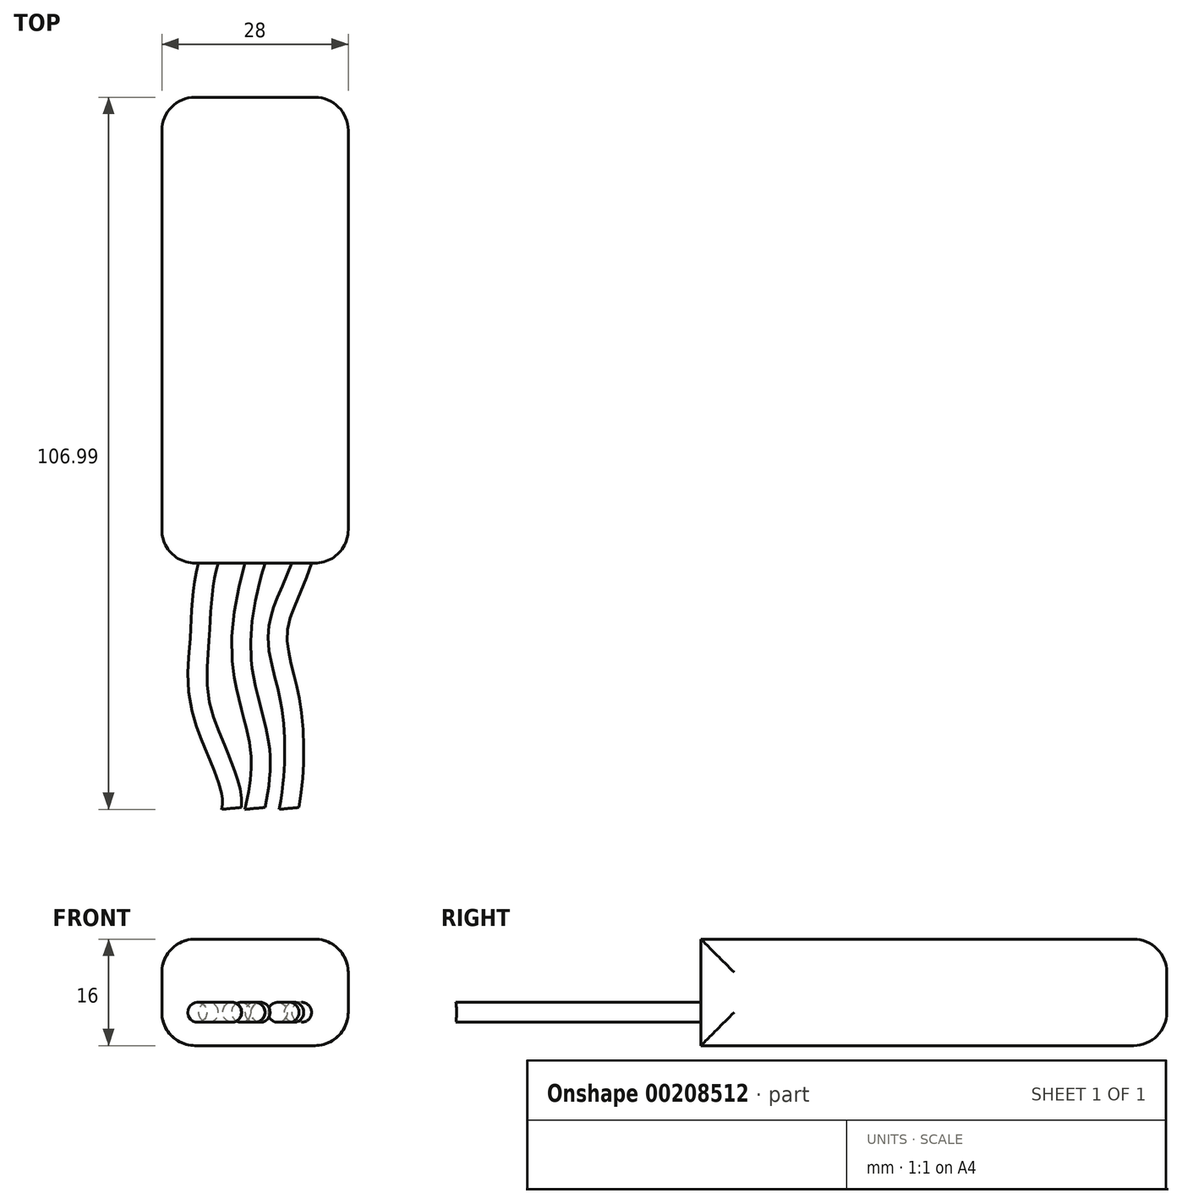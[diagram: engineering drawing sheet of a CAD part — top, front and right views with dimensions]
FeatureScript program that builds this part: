
annotation { "Feature Type Name" : "Feature", "Feature Type Description" : "" }
export const myFeature = defineFeature(function(context is Context, id is Id, definition is map)
    precondition{}
    {
        {
            var Q0;
            Q0=qCreatedBy(makeId("Top.planeOp"),FACE);
            var sketch = newSketch(context, id + "F0", { "sketchPlane" : qUnion([Q0])});
            skLineSegment(sketch, "E0.bottom", {"start": v(14, -35) * mm, "end": v(-14, -35) * mm});
            skLineSegment(sketch, "E0.top", {"start": v(14, 35) * mm, "end": v(-14, 35) * mm});
            skLineSegment(sketch, "E0.left", {"start": v(14, -35) * mm, "end": v(14, 35) * mm});
            skLineSegment(sketch, "E0.right", {"start": v(-14, -35) * mm, "end": v(-14, 35) * mm});
            skPoint(sketch, "E0.middle", {"position": v(0, 0) * mm});
            skSolve(sketch);
        }
        {
            var Q0;
            Q0 = qSketchRegion(id + "F0", true);
            extrude(context, id + "F1", {"entities" : qUnion([Q0]), "depth" : 16 * mm});
        }
        {
            var Q0;
            Q0=makeQuery(id+"F1.opExtrude","SWEPT_FACE",FACE,{"disambiguationData":[OSD([sQuery(id+"F0.wireOp",EDGE,"E0.left")])]});
            var Q1;
            Q1=makeQuery(id+"F1.opExtrude","SWEPT_FACE",FACE,{"disambiguationData":[OSD([sQuery(id+"F0.wireOp",EDGE,"E0.right")])]});
            var Q2;
            Q2=makeQuery(id+"F1.opExtrude","SWEPT_FACE",FACE,{"disambiguationData":[OSD([sQuery(id+"F0.wireOp",EDGE,"E0.top")])]});
            fillet(context, id + "F2", {"entities" : qUnion([Q0, Q1, Q2]), "radius" : 5 * mm, "tangentPropagation" : true, "allowEdgeOverflow" : false});
        }
        {
            var Q0;
            Q0=makeQuery(id+"F1.opExtrude","SWEPT_FACE",FACE,{"disambiguationData":[OSD([sQuery(id+"F0.wireOp",EDGE,"E0.bottom")])]});
            var sketch = newSketch(context, id + "F3", { "sketchPlane" : qUnion([Q0])});
            skCircle(sketch, "E1", {"center": v(0, 5) * mm, "radius": 1.5 * mm});
            skCircle(sketch, "E2", {"center": v(7, 5) * mm, "radius": 1.5 * mm});
            skCircle(sketch, "E3", {"center": v(-7, 5) * mm, "radius": 1.5 * mm});
            skSolve(sketch);
        }
        {
            var Q0;
            Q0=makeQuery(id+"F1.opExtrude","CAP_FACE",FACE,{"disambiguationData":[OSD([sQuery(id+"F0.wireOp",EDGE,"E0.bottom"),sQuery(id+"F0.wireOp",EDGE,"E0.top"),sQuery(id+"F0.wireOp",EDGE,"E0.left"),sQuery(id+"F0.wireOp",EDGE,"E0.right")])],"isStart":false});
            var Q1;
            Q1=sQuery(id+"F3.wireOp",VERTEX,"E1.center");
            cPlane(context, id + "F4", {"entities" : qUnion([Q0, Q1]), "cplaneType" : CPlaneType.PLANE_POINT, "offset" : 25 * mm, "width" : 150 * mm, "height" : 150 * mm});
        }
        {
            var Q0;
            Q0=qCreatedBy(id+"F4.planeOp",FACE);
            var sketch = newSketch(context, id + "F5", { "sketchPlane" : qUnion([Q0])});
            skFitSpline(sketch, "E4", {"points": [v(0, -35) * mm, v(-2, -49.56) * mm, v(0.74, -62.9) * mm, v(0, -71.85) * mm], "startDerivative": vector(-10.09, -32.94) * mm, "endDerivative": vector(-5.76, -27.82) * mm});
            skFitSpline(sketch, "E5", {"points": [v(-7, -35) * mm, v(-8.33, -46.63) * mm, v(-7.9, -57.6) * mm, v(-3.53, -71.85) * mm], "startDerivative": vector(-10.09, -32.94) * mm, "endDerivative": vector(-5.76, -27.82) * mm});
            skFitSpline(sketch, "E6", {"points": [v(7, -35) * mm, v(3.45, -45.1) * mm, v(5.46, -56.75) * mm, v(5.11, -71.85) * mm], "startDerivative": vector(-10.09, -32.94) * mm, "endDerivative": vector(-5.76, -27.82) * mm});
            skSolve(sketch);
        }
        {
            var Q0;
            Q0=makeQuery(id+"F3.imprint","IMPRINT",FACE,{"disambiguationData":[TD([[makeQuery(id+"F3.imprint","IMPRINT",EDGE,{"derivedFrom":sQuery(id+"F3.wireOp",EDGE,"E1")}),1.0]])]});
            var Q1;
            Q1=sQuery(id+"F5.wireOp",EDGE,"E4");
            sweep(context, id + "F6", {"operationType" : NewBodyOperationType.ADD, "profiles" : qUnion([Q0]), "path" : qUnion([Q1])});
        }
        {
            var Q0;
            Q0=makeQuery(id+"F3.imprint","IMPRINT",FACE,{"disambiguationData":[TD([[makeQuery(id+"F3.imprint","IMPRINT",EDGE,{"derivedFrom":sQuery(id+"F3.wireOp",EDGE,"E3")}),1.0]])]});
            var Q1;
            Q1=sQuery(id+"F5.wireOp",EDGE,"E5");
            sweep(context, id + "F7", {"operationType" : NewBodyOperationType.ADD, "profiles" : qUnion([Q0]), "path" : qUnion([Q1])});
        }
        {
            var Q0;
            Q0=makeQuery(id+"F3.imprint","IMPRINT",FACE,{"disambiguationData":[TD([[makeQuery(id+"F3.imprint","IMPRINT",EDGE,{"derivedFrom":sQuery(id+"F3.wireOp",EDGE,"E2")}),1.0]])]});
            var Q1;
            Q1=sQuery(id+"F5.wireOp",EDGE,"E6");
            sweep(context, id + "F8", {"operationType" : NewBodyOperationType.ADD, "profiles" : qUnion([Q0]), "path" : qUnion([Q1])});
        }
    });
